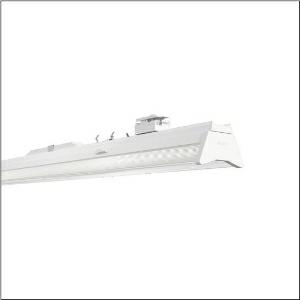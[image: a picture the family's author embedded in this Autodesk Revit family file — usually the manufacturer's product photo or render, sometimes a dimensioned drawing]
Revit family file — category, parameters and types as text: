
# Revit family: licross_11_performance_ho_51tm16dn4fxm
name_source: partatom
category: Lighting Fixtures
units: mm (PartAtom-declared; Revit-internal decimal feet)

## family parameters
Cut with Voids When Loaded = No
Host = Face
Light Source = No
Part Type = Normal
Room Calculation Point = No
Round Connector Dimension = Use Diameter
Shared = No

## types (1)
- --- (1 x LED, 15460 lm, 87.3 W, 4000K)
    Apparent Load = 87 VA
    CIE Flux Codes = 63 87 95 78 100
    Color Rendering = 80
    Color Temperature = 4000K
    Default Elevation = 1800 mm
    Description = Licross 11 Performance HO, luminaire insert, of sheet steel, galvanised, coil coated, white, length: 1.500mm, width: 120mm, height: 123mm, LED rated luminous flux: 15.460lm, light colour: 840, SDCM (Standard Deviation of Colour Matching)MacAdam ≤ 2 SDCM (initial), control gear: DALI 2, with plug, 5-pole, with phase selection, mains connection: 220..240V, AC, 50/60Hz, rated input power: 87W, internal wiring halogen-free, primary light control with lens, of plastic, primary optical cover: cover, of PMMA, light emission: direct/indirect distribution, primary light characteristic: symmetric, protection rating (complete): IP40, insulation class (complete): insulation class I (protective earthing), certification: CE, ENEC, VDE, UKCA, protection symbol: D if used in an environment without relevant dust loads with corresponding accessories, impact resistance: IK06, permissible ambient temperature for indoor applications: -25..+30°C, corresponds to IFS (International Featured Standards) requirements for safety and quality in the food industry, reducing of maximum allowable ambient temperature of 5°C with ceiling mounting, LABS conformity tested according to VDMA 24364:2018-05, The light source and the operating device comply with the requirements of the Ecodesign Regulation (EU) 2019/2020 and are replaceable in accordance with this regulation, packaging unit: 1 piece
    Height = 114 mm
    Lamp = 1 x LED
    Lamp Light Flux = 15460 lm
    Lamp Power = 87.3 W
    Lamp count = 1
    Length = 1500 mm
    Luminous efficacy = 177 lm/W
    Manufacturer = Siteco
    ModVariant = No
    Model = 51TM16DN4FXM
    Mounting Place = Ceiling
    Mounting Type = Pendant
    Number of Poles = 1
    OnlyDefault = Yes
    Power Factor = 1
    Product Name = Licross 11 Performance HO
    Product group = luminaire insert | ceiling pendant
    ProductGroupID = 901
    Protection Class = Protection class I
    Protection Degree = IP 40
    RLX_Detail_Level = 1
    RLX_Emergency_Light_Flux = 0 lm
    RLX_Emergency_Type = 0
    RLX_Emergency_Type_DB = No
    RlxData = <blob elided: 34293 chars, md5=c1086c80>
    Socket = socket
    Standby Power = 0 W
    System Light Flux = 15460 lm
    System Power = 87 W
    Type Comments = factory setting: luminous flux: 100 % | dim-lin: 254 | 589 mA
    Type Image = l_1256138.jpg
    URL = http://relux.com
    VarID = @adj_102977
    Voltage = 0 V
    Weight = 0.00 kg
    Width = 120 mm

## geometry (parser evidence)
native form markers: Blend x4, Sweep x12
no freeform markers — native parametric forms only
